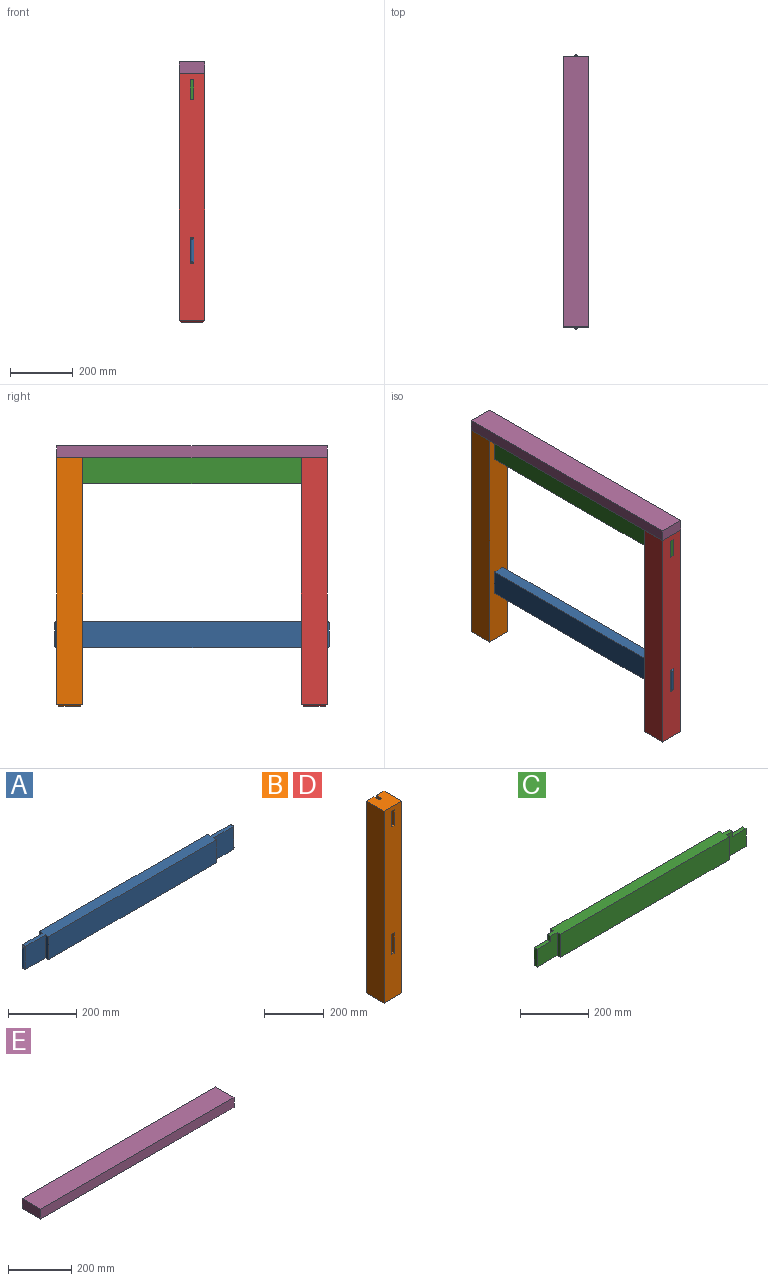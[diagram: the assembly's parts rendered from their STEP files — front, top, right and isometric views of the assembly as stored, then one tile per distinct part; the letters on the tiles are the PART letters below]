
ASSEMBLY  parts=5 mates=12
PART A: 18 faces, bbox 876.3x38.1x82.6 mm
  f0: plane 82.55x12.7mm, normal (1,0,0), area 1048.4mm2, adj f1,f9,f10,f11
  f1: plane 82.55x82.55mm, normal (0,-1,0), area 6814.5mm2, adj f0,f10,f11,f16
  f2: plane 82.55x82.55mm, normal (0,1,0), area 6814.5mm2, adj f3,f10,f11,f16
  f3: plane 82.55x12.7mm, normal (1,0,0), area 1048.4mm2, adj f2,f4,f10,f11
  f4: plane 698.5x82.55mm, normal (0,1,0), area 57661.2mm2, adj f3,f5,f10,f11
  f5: plane 82.55x12.7mm, normal (-1,0,0), area 1048.4mm2, adj f4,f6,f10,f11
  f6: plane 82.55x82.55mm, normal (0,1,0), area 6814.5mm2, adj f5,f10,f11,f13
  f7: plane 82.55x82.55mm, normal (0,-1,0), area 6814.5mm2, adj f8,f10,f11,f13
  f8: plane 82.55x12.7mm, normal (-1,0,0), area 1048.4mm2, adj f7,f9,f10,f11
  f9: plane 698.5x82.55mm, normal (0,-1,0), area 57661.2mm2, adj f0,f8,f10,f11
  f10: plane 863.6x38.1mm, normal (0,0,1), area 28709.6mm2, adj f0,f1,f2,f3,f4,f5,f6,f7
  f11: plane 863.6x38.1mm, normal (0,0,-1), area 28709.6mm2, adj f0,f1,f2,f3,f4,f5,f6,f7
  f12: cylinder r=6.35mm len=12.7mm, axis (0,1,0), area 80.6mm2, adj f10,f13
  f13: cylinder r=6.35mm len=82.55mm, axis (0,0,-1), area 1554.7mm2, adj f6,f7,f12,f14
  f14: cylinder r=6.35mm len=12.7mm, axis (0,-1,0), area 80.6mm2, adj f11,f13
  f15: cylinder r=6.35mm len=12.7mm, axis (0,-1,0), area 80.6mm2, adj f10,f16
  f16: cylinder r=6.35mm len=82.55mm, axis (0,0,1), area 1554.7mm2, adj f1,f2,f15,f17
  f17: cylinder r=6.35mm len=12.7mm, axis (0,1,0), area 80.6mm2, adj f11,f16
PART B: 19 faces, bbox 82.6x82.6x793.8 mm
  f0: plane 787.4x82.55mm, normal (0,1,0), area 62903.1mm2, adj f3,f4,f5,f9,f11,f12,f13,f15
  f1: plane 787.4x82.55mm, normal (0,-1,0), area 63145mm2, adj f3,f4,f5,f8,f11,f12,f13,f14
  f2: plane 19.05x12.7mm, normal (0,1,0), area 241.9mm2, adj f3,f11,f12,f14
  f3: plane 82.55x82.55mm, normal (0,0,1), area 6491.9mm2, adj f0,f1,f2,f4,f5,f11,f12
  f4: plane 787.4x82.55mm, normal (-1,0,0), area 64999.9mm2, adj f0,f1,f3,f7
  f5: plane 787.4x82.55mm, normal (1,0,0), area 64999.9mm2, adj f0,f1,f3,f10
  f6: plane 69.85x69.85mm, normal (0,0,-1), area 4879mm2, adj f7,f8,f9,f10
  f7: plane 82.55x6.35mm, normal (-0.71,0,-0.71), area 684.3mm2, adj f4,f6,f8,f9
  f8: plane 82.55x6.35mm, normal (0,-0.71,-0.71), area 684.3mm2, adj f1,f6,f7,f10
  f9: plane 82.55x6.35mm, normal (0,0.71,-0.71), area 684.3mm2, adj f0,f6,f7,f10
  f10: plane 82.55x6.35mm, normal (0.71,0,-0.71), area 684.3mm2, adj f5,f6,f8,f9
  f11: plane 82.55x82.55mm, normal (1,0,0), area 5725.8mm2, adj f0,f1,f2,f3,f13,f14
  f12: plane 82.55x82.55mm, normal (-1,0,0), area 5725.8mm2, adj f0,f1,f2,f3,f13,f14
  f13: plane 82.55x12.7mm, normal (0,0,1), area 1048.4mm2, adj f0,f1,f11,f12
  f14: plane 57.15x12.7mm, normal (0,0,-1), area 725.8mm2, adj f1,f2,f11,f12
  f15: plane 82.55x12.7mm, normal (0,0,-1), area 1048.4mm2, adj f0,f1,f16,f18
  f16: plane 82.55x82.55mm, normal (-1,0,0), area 6814.5mm2, adj f0,f1,f15,f17
  f17: plane 82.55x12.7mm, normal (0,0,1), area 1048.4mm2, adj f0,f1,f16,f18
  f18: plane 82.55x82.55mm, normal (1,0,0), area 6814.5mm2, adj f0,f1,f15,f17
PART C: 18 faces, bbox 863.6x38.1x82.6 mm
  f0: plane 82.55x82.55mm, normal (0,-1,0), area 5725.8mm2, adj f3,f4,f5,f13,f16,f17
  f1: plane 82.55x82.55mm, normal (0,1,0), area 5725.8mm2, adj f3,f5,f6,f13,f16,f17
  f2: plane 82.55x82.55mm, normal (0,-1,0), area 5725.8mm2, adj f3,f10,f11,f13,f14,f15
  f3: plane 749.3x38.1mm, normal (0,0,1), area 27258mm2, adj f0,f1,f2,f4,f6,f7,f8,f9
  f4: plane 82.55x12.7mm, normal (1,0,0), area 1048.4mm2, adj f0,f3,f12,f13
  f5: plane 63.5x12.7mm, normal (1,0,0), area 806.5mm2, adj f0,f1,f13,f17
  f6: plane 82.55x12.7mm, normal (1,0,0), area 1048.4mm2, adj f1,f3,f7,f13
  f7: plane 698.5x82.55mm, normal (0,1,0), area 57661.2mm2, adj f3,f6,f8,f13
  f8: plane 82.55x12.7mm, normal (-1,0,0), area 1048.4mm2, adj f3,f7,f9,f13
  f9: plane 82.55x82.55mm, normal (0,1,0), area 5725.8mm2, adj f3,f8,f10,f13,f14,f15
  f10: plane 63.5x12.7mm, normal (-1,0,0), area 806.5mm2, adj f2,f9,f13,f15
  f11: plane 82.55x12.7mm, normal (-1,0,0), area 1048.4mm2, adj f2,f3,f12,f13
  f12: plane 698.5x82.55mm, normal (0,-1,0), area 57661.2mm2, adj f3,f4,f11,f13
  f13: plane 863.6x38.1mm, normal (0,0,-1), area 28709.6mm2, adj f0,f1,f2,f4,f5,f6,f7,f8
  f14: plane 19.05x12.7mm, normal (-1,0,0), area 241.9mm2, adj f2,f3,f9,f15
  f15: plane 57.15x12.7mm, normal (0,0,1), area 725.8mm2, adj f2,f9,f10,f14
  f16: plane 19.05x12.7mm, normal (1,0,0), area 241.9mm2, adj f0,f1,f3,f17
  f17: plane 57.15x12.7mm, normal (0,0,1), area 725.8mm2, adj f0,f1,f5,f16
PART D: same geometry as B
PART E: 6 faces, bbox 863.6x82.6x38.1 mm
  f0: plane 863.6x38.1mm, normal (0,-1,0), area 32903.2mm2, adj f1,f3,f4,f5
  f1: plane 82.55x38.1mm, normal (1,0,0), area 3145.2mm2, adj f0,f2,f4,f5
  f2: plane 863.6x38.1mm, normal (0,1,0), area 32903.2mm2, adj f1,f3,f4,f5
  f3: plane 82.55x38.1mm, normal (-1,0,0), area 3145.2mm2, adj f0,f2,f4,f5
  f4: plane 863.6x82.55mm, normal (0,0,1), area 71290.2mm2, adj f0,f1,f2,f3
  f5: plane 863.6x82.55mm, normal (0,0,-1), area 71290.2mm2, adj f0,f1,f2,f3
PLACE A rot(axis=(-0.71,-0.71,0),180deg) t=(-448.31,145.79,517.98)mm
PLACE B rot(axis=(0,0,1),180deg) t=(-448.31,536.31,248.1)mm
PLACE C rot(axis=(0,0,-1),90deg) t=(-448.31,145.79,959.3)mm
PLACE D t=(-448.31,-244.74,248.1)mm
PLACE E rot(axis=(-0.71,0.71,0),180deg) t=(-448.31,145.79,1079.95)mm
MATE planar C.f9 <-> B.f11  axis (1,0,0) through (-441.96,533.9,994.54)mm
MATE planar E.f3 <-> B.f1  axis (0,1,0) through (-489.58,577.59,1060.9)mm
MATE planar D.f16 <-> A.f6  axis (-1,0,0) through (-441.96,-244.74,476.7)mm
MATE planar C.f5 <-> D.f1  axis (0,-1,0) through (-448.31,-286.01,991.05)mm
MATE planar C.f3 <-> D.f3  axis (0,0,1) through (-429.26,145.79,1041.85)mm
MATE planar B.f3 <-> C.f3  axis (0,0,1) through (-489.58,536.31,1041.85)mm
MATE planar C.f1 <-> D.f12  axis (1,0,0) through (-441.96,-242.32,994.54)mm
MATE planar B.f0 <-> C.f8  axis (0,-1,0) through (-441.96,495.04,1000.58)mm
MATE planar E.f2 <-> B.f5  axis (-1,0,0) through (-489.58,577.59,1041.85)mm
MATE planar E.f4 <-> C.f3  axis (0,0,-1) through (-448.31,145.79,1041.85)mm
MATE planar A.f11 <-> B.f15  axis (0,0,1) through (-448.31,145.79,517.98)mm
MATE planar A.f0 <-> B.f0  axis (0,1,0) through (-461.01,495.04,476.7)mm
